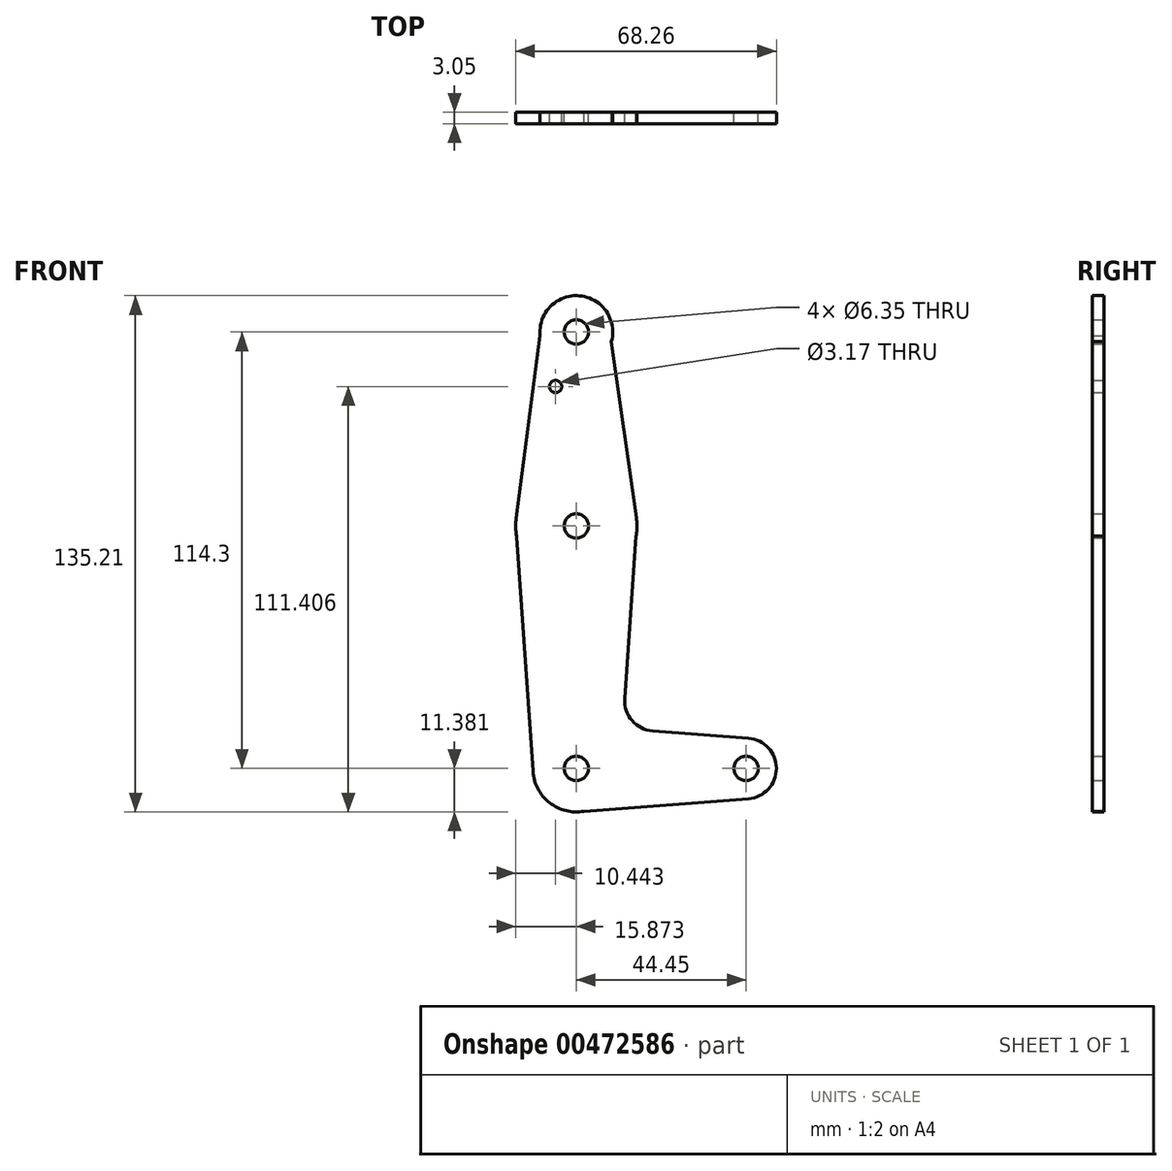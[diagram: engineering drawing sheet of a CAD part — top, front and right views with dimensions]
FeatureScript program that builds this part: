
annotation { "Feature Type Name" : "Feature", "Feature Type Description" : "" }
export const myFeature = defineFeature(function(context is Context, id is Id, definition is map)
    precondition{}
    {
        {
            var Q0;
            Q0=qCreatedBy(makeId("Front.planeOp"),FACE);
            var sketch = newSketch(context, id + "F0", { "sketchPlane" : qUnion([Q0])});
            skCircle(sketch, "E0", {"center": v(-39.27, 79.38) * mm, "radius": 9.53 * mm});
            skLineSegment(sketch, "E1", {"start": v(-39.27, 79.38) * mm, "end": v(-39.27, -34.92) * mm, "construction": true});
            skLineSegment(sketch, "E2", {"start": v(-39.27, -34.92) * mm, "end": v(5.18, -34.92) * mm, "construction": true});
            skCircle(sketch, "E3", {"center": v(-39.27, -34.92) * mm, "radius": 11.39 * mm});
            skCircle(sketch, "E4", {"center": v(5.18, -34.92) * mm, "radius": 7.94 * mm});
            skCircle(sketch, "E5", {"center": v(-39.27, 28.58) * mm, "radius": 15.88 * mm});
            skLineSegment(sketch, "E6", {"start": v(-48.74, 78.4) * mm, "end": v(-55, 30.65) * mm});
            skLineSegment(sketch, "E7", {"start": v(-30.08, 76.86) * mm, "end": v(-23.55, 30.81) * mm});
            skLineSegment(sketch, "E8", {"start": v(-23.62, 25.9) * mm, "end": v(-26.58, -16.6) * mm});
            skLineSegment(sketch, "E9", {"start": v(-54.87, 25.65) * mm, "end": v(-50.63, -35.7) * mm});
            skLineSegment(sketch, "E10", {"start": v(-19.26, -25.08) * mm, "end": v(5.8, -27) * mm});
            skLineSegment(sketch, "E11", {"start": v(-39.55, -46.3) * mm, "end": v(5.79, -42.83) * mm});
            skCircle(sketch, "E12", {"center": v(-39.27, 79.38) * mm, "radius": 3.18 * mm});
            skCircle(sketch, "E13", {"center": v(-39.27, 28.58) * mm, "radius": 3.18 * mm});
            skCircle(sketch, "E14", {"center": v(-39.27, -34.92) * mm, "radius": 3.18 * mm});
            skCircle(sketch, "E15", {"center": v(5.18, -34.92) * mm, "radius": 3.18 * mm});
            skArc(sketch, "E16.filletArc", {"start": v(-26.58, -16.6) * mm, "mid": v(-24.67, -22.34) * mm, "end": v(-19.26, -25.08) * mm});
            skCircle(sketch, "E17", {"center": v(-44.7, 65.1) * mm, "radius": 1.59 * mm});
            skSolve(sketch);
        }
        {
            var Q0;
            Q0 = qSketchRegion(id + "F0", true);
            extrude(context, id + "F1", {"entities" : qUnion([Q0]), "depth" : 3.05 * mm});
        }
    });
